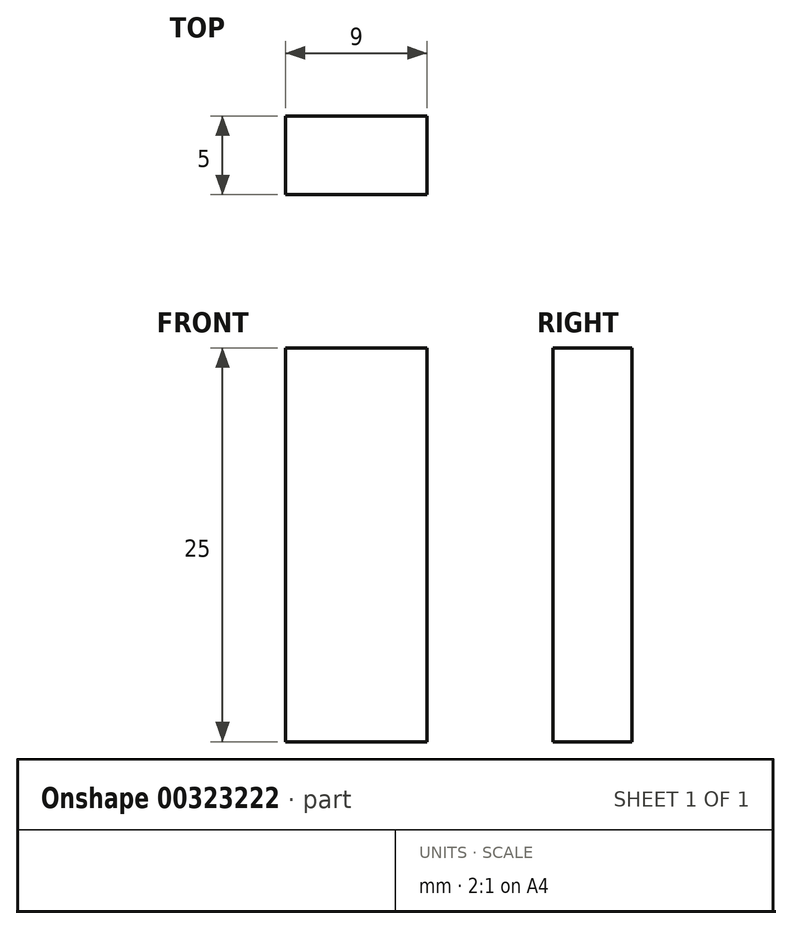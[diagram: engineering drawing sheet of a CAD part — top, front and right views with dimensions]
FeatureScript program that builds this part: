
annotation { "Feature Type Name" : "Feature", "Feature Type Description" : "" }
export const myFeature = defineFeature(function(context is Context, id is Id, definition is map)
    precondition{}
    {
        {
            var Q0;
            Q0=qCreatedBy(makeId("Right.planeOp"),FACE);
            var sketch = newSketch(context, id + "F0", { "sketchPlane" : qUnion([Q0])});
            skLineSegment(sketch, "E0", {"start": v(5, 0) * mm, "end": v(5, 10) * mm});
            skLineSegment(sketch, "E1", {"start": v(5, 10) * mm, "end": v(0, 10) * mm});
            skLineSegment(sketch, "E2", {"start": v(0, 10) * mm, "end": v(0, 0) * mm});
            skLineSegment(sketch, "E3", {"start": v(0, 0) * mm, "end": v(5, 0) * mm});
            skSolve(sketch);
        }
        {
            var Q0;
            Q0=qSketchRegion(id+"F0",true);
            extrude(context, id + "F1", {"entities" : qUnion([Q0]), "depth" : 9 * mm});
        }
        {
            var Q0;
            Q0=makeQuery(id+"F1.opExtrude","SWEPT_FACE",FACE,{"disambiguationData":[OSD([sQuery(id+"F0.wireOp",EDGE,"E3")])]});
            extrude(context, id + "F2", {"entities" : qUnion([Q0]), "operationType" : NewBodyOperationType.ADD, "depth" : 15 * mm});
        }
        {
            var Q0;
            {var subQ0=sQuery(id+"F0.wireOp",EDGE,"E3");Q0=makeQuery(id+"F2.opExtrude","CAP_EDGE",EDGE,{"disambiguationData":[OSD([subQ0]),TDD([makeQuery(id+"F1.opExtrude","CAP_EDGE",EDGE,{"disambiguationData":[OSD([subQ0])],"isStart":true})])],"isStart":false});}
            var Q1;
            Q1=qCreatedBy(makeId("Right.planeOp"),FACE);
            cPlane(context, id + "F3", {"entities" : qUnion([Q0, Q1]), "cplaneType" : CPlaneType.LINE_ANGLE, "offset" : 25 * mm, "angle" : 30 * degree, "oppositeDirection" : true, "width" : 150 * mm, "height" : 150 * mm});
        }
    });
